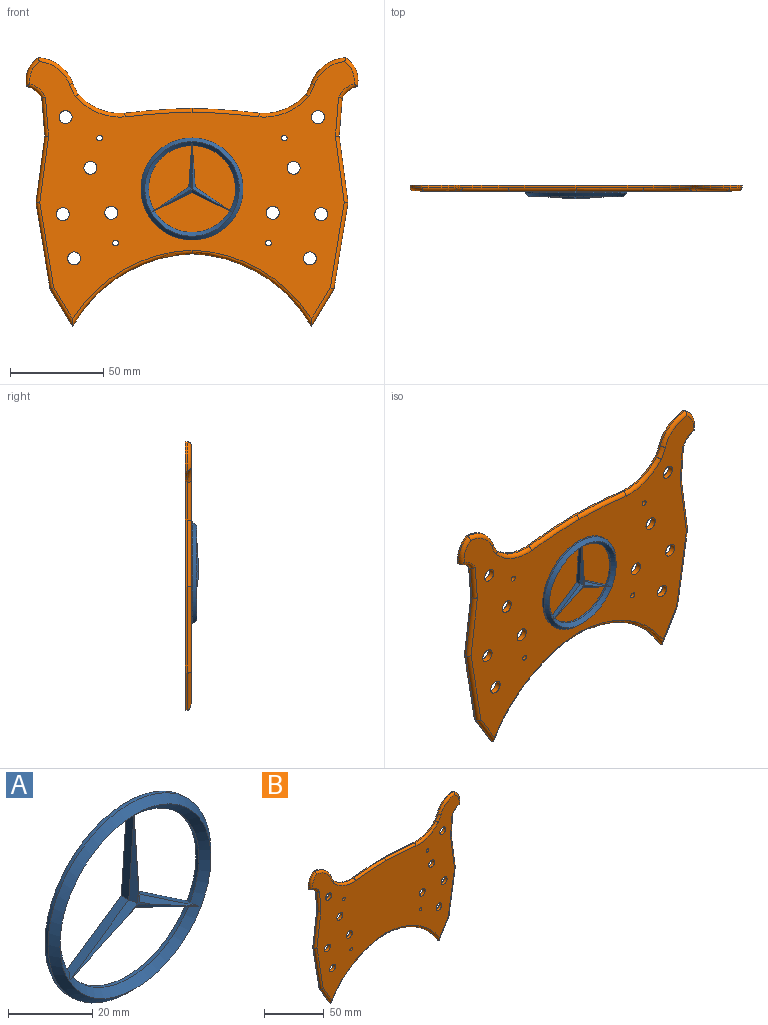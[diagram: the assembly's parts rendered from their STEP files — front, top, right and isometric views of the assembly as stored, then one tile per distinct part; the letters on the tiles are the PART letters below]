
ASSEMBLY  parts=2 mates=2
PART A: 20 faces, bbox 54.6x4x54.6 mm
  f0: cylinder r=23.31mm len=40.24mm, axis (0,1,0), area 48.5mm2, adj f4,f5,f9,f11
  f1: cylinder r=23.31mm len=34.85mm, axis (0,1,0), area 48.5mm2, adj f4,f5,f8,f10
  f2: cylinder r=23.31mm len=34.85mm, axis (0,1,0), area 48.5mm2, adj f4,f5,f7,f12
  f3: cylinder r=27.31mm len=54.63mm, axis (0,1,0), area 171.6mm2, adj f4,f6
  f4: plane 54.63x54.63mm, normal (0,1,0), area 766.9mm2, adj f0,f1,f2,f3,f7,f8,f9,f10
  f5: cone r=23.31mm half-angle=45deg, axis (0,-1,0), area 430.9mm2, adj f0,f1,f2,f6,f7,f8,f9,f10
  f6: cone r=25.31mm half-angle=45deg, axis (0,1,0), area 467.6mm2, adj f3,f5
  f7: plane 23.82x2.5mm, normal (1,0,0.07), area 57.1mm2, adj f2,f4,f5,f12,f17
  f8: plane 23.82x2.5mm, normal (-1,0,0.07), area 57.1mm2, adj f1,f4,f5,f10,f19
  f9: plane 21.48x10.44mm, normal (-0.44,0,-0.9), area 57.1mm2, adj f0,f4,f5,f11,f14
  f10: plane 19.78x13.38mm, normal (-0.56,0,0.83), area 57.1mm2, adj f1,f4,f5,f8,f18
  f11: plane 21.48x10.44mm, normal (0.44,0,-0.9), area 57.1mm2, adj f0,f4,f5,f9,f16
  f12: plane 19.78x13.38mm, normal (0.56,0,0.83), area 57.1mm2, adj f2,f4,f5,f7,f15
  f13: plane 7.28x6.31mm, normal (0,-1,0), area 3.6mm2, adj f14,f15,f16,f17,f18,f19
  f14: plane 21.52x12.11mm, normal (-0.31,-0.71,-0.64), area 30.1mm2, adj f5,f9,f13,f15,f16
  f15: plane 21.23x13.42mm, normal (0.4,-0.71,0.59), area 30.1mm2, adj f5,f12,f13,f14,f17
  f16: plane 21.52x12.11mm, normal (0.31,-0.71,-0.64), area 30.1mm2, adj f5,f11,f13,f14,f18
  f17: plane 24.68x1.73mm, normal (0.71,-0.71,0.05), area 30.1mm2, adj f5,f7,f13,f15,f19
  f18: plane 21.23x13.42mm, normal (-0.4,-0.71,0.59), area 30.1mm2, adj f5,f10,f13,f16,f19
  f19: plane 24.68x1.73mm, normal (-0.71,-0.71,0.05), area 30.1mm2, adj f5,f8,f13,f17,f18
PART B: 60 faces, bbox 180.3x3.4x145.7 mm
  f0: cylinder r=21.18mm len=18.59mm, axis (0,1,0), area 24.4mm2, adj f1,f21,f23,f43
  f1: cylinder r=14.27mm len=15.48mm, axis (0,1,0), area 17.8mm2, adj f0,f2,f23,f41
  f2: cylinder r=12.43mm len=8.03mm, axis (0,1,0), area 10.5mm2, adj f1,f3,f23,f39
  f3: plane 20.2x1.64mm, normal (-1,0,-0.08), area 20.3mm2, adj f2,f4,f23,f37
  f4: plane 35.67x4.72mm, normal (-0.99,0,0.13), area 36mm2, adj f3,f5,f23,f35
  f5: plane 46.36x7.54mm, normal (-0.99,0,-0.16), area 47mm2, adj f4,f6,f23,f33
  f6: plane 19.96x12.1mm, normal (-0.86,0,-0.52), area 23.3mm2, adj f5,f7,f23,f31
  f7: cylinder r=76.53mm len=63.97mm, axis (0,1,0), area 78.2mm2, adj f6,f8,f23,f29
  f8: cylinder r=76.53mm len=63.97mm, axis (0,1,0), area 78.2mm2, adj f7,f9,f23,f27
  f9: plane 19.96x12.1mm, normal (0.86,0,-0.52), area 23.3mm2, adj f8,f10,f23,f25
  f10: plane 46.36x7.54mm, normal (0.99,0,-0.16), area 47mm2, adj f9,f11,f23,f24
  f11: plane 35.67x4.72mm, normal (0.99,0,0.13), area 36mm2, adj f10,f12,f23,f26
  f12: plane 20.2x1.64mm, normal (1,0,-0.08), area 20.3mm2, adj f11,f13,f23,f28
  f13: cylinder r=12.43mm len=8.03mm, axis (0,1,0), area 10.5mm2, adj f12,f14,f23,f30
  f14: cylinder r=14.27mm len=15.48mm, axis (0,1,0), area 17.8mm2, adj f13,f15,f23,f32
  f15: cylinder r=21.18mm len=18.59mm, axis (0,1,0), area 24.4mm2, adj f14,f16,f23,f34
  f16: cylinder r=24.05mm len=5.87mm, axis (0,1,0), area 6.6mm2, adj f15,f17,f23,f36
  f17: cylinder r=29.8mm len=24.85mm, axis (0,1,0), area 27.9mm2, adj f16,f18,f23,f38
  f18: cylinder r=331.42mm len=36.04mm, axis (0,1,0), area 36.2mm2, adj f17,f19,f23,f40
  f19: cylinder r=331.42mm len=36.04mm, axis (0,1,0), area 36.2mm2, adj f18,f20,f23,f42
  f20: cylinder r=29.8mm len=24.85mm, axis (0,1,0), area 27.9mm2, adj f19,f21,f23,f44
  f21: cylinder r=24.05mm len=5.87mm, axis (0,1,0), area 6.6mm2, adj f0,f20,f23,f45
  f22: plane 173.95x138.02mm, normal (0,-1,0), area 14175.4mm2, adj f24,f25,f26,f27,f28,f29,f30,f31
  f23: plane 177.95x143.95mm, normal (0,1,0), area 15469.2mm2, adj f0,f1,f2,f3,f4,f5,f6,f7
  f24: cylinder r=2mm len=46.68mm, axis (-0.16,0,-0.99), area 146.8mm2, adj f10,f22,f25,f26
  f25: cylinder r=2mm len=21mm, axis (-0.52,0,-0.86), area 69mm2, adj f9,f22,f24,f27
  f26: cylinder r=2mm len=36.14mm, axis (0.13,0,-0.99), area 112.9mm2, adj f11,f22,f24,f28
  f27: torus R=78.53mm, axis (0,-1,0), area 244.2mm2, adj f8,f22,f25,f29
  f28: cylinder r=2mm len=20.96mm, axis (-0.08,0,-1), area 64.4mm2, adj f12,f22,f26,f30
  f29: torus R=78.53mm, axis (0,-1,0), area 244.2mm2, adj f7,f22,f27,f31
  f30: torus R=14.43mm, axis (0,-1,0), area 34mm2, adj f13,f22,f28,f32
  f31: cylinder r=2mm len=21mm, axis (-0.52,0,0.86), area 69mm2, adj f6,f22,f29,f33
  f32: torus R=12.27mm, axis (0,-1,0), area 51mm2, adj f14,f22,f30,f34
  f33: cylinder r=2mm len=46.68mm, axis (-0.16,0,0.99), area 146.8mm2, adj f5,f22,f31,f35
  f34: torus R=19.18mm, axis (0,-1,0), area 73.3mm2, adj f15,f22,f32,f36
  f35: cylinder r=2mm len=36.14mm, axis (0.13,0,0.99), area 112.9mm2, adj f4,f22,f33,f37
  f36: torus R=26.05mm, axis (0,-1,0), area 21.4mm2, adj f16,f22,f34,f38
  f37: cylinder r=2mm len=20.96mm, axis (-0.08,0,1), area 64.4mm2, adj f3,f22,f35,f39
  f38: torus R=31.8mm, axis (0,-1,0), area 89.9mm2, adj f17,f22,f36,f40
  f39: torus R=14.43mm, axis (0,-1,0), area 34mm2, adj f2,f22,f37,f41
  f40: torus R=329.42mm, axis (0,-1,0), area 113.3mm2, adj f18,f22,f38,f42
  f41: torus R=12.27mm, axis (0,-1,0), area 51mm2, adj f1,f22,f39,f43
  f42: torus R=329.42mm, axis (0,-1,0), area 113.3mm2, adj f19,f22,f40,f44
  f43: torus R=19.18mm, axis (0,-1,0), area 73.3mm2, adj f0,f22,f41,f45
  f44: torus R=31.8mm, axis (0,-1,0), area 89.9mm2, adj f20,f22,f42,f45
  f45: torus R=26.05mm, axis (0,-1,0), area 21.4mm2, adj f21,f22,f43,f44
  f46: cylinder r=1.5mm len=3mm, axis (0,1,0), area 28.3mm2, adj f22,f23
  f47: cylinder r=1.5mm len=3mm, axis (0,1,0), area 28.3mm2, adj f22,f23
  f48: cylinder r=1.5mm len=3mm, axis (0,1,0), area 28.3mm2, adj f22,f23
  f49: cylinder r=1.5mm len=3mm, axis (0,1,0), area 28.3mm2, adj f22,f23
  f50: cylinder r=3.5mm len=7mm, axis (0,1,0), area 66mm2, adj f22,f23
  f51: cylinder r=3.5mm len=7mm, axis (0,1,0), area 66mm2, adj f22,f23
  f52: cylinder r=3.5mm len=7mm, axis (0,1,0), area 66mm2, adj f22,f23
  f53: cylinder r=3.5mm len=7mm, axis (0,1,0), area 66mm2, adj f22,f23
  f54: cylinder r=3.5mm len=7mm, axis (0,1,0), area 66mm2, adj f22,f23
  f55: cylinder r=3.5mm len=7mm, axis (0,1,0), area 66mm2, adj f22,f23
  f56: cylinder r=3.5mm len=7mm, axis (0,1,0), area 66mm2, adj f22,f23
  f57: cylinder r=3.5mm len=7mm, axis (0,1,0), area 66mm2, adj f22,f23
  f58: cylinder r=3.5mm len=7mm, axis (0,1,0), area 66mm2, adj f22,f23
  f59: cylinder r=3.5mm len=7mm, axis (0,1,0), area 66mm2, adj f22,f23
PLACE A t=(4.03,47.64,96.39)mm
PLACE B t=(4.03,50.64,103.01)mm
MATE planar A.f3 <-> B.f22  axis (0,1,0) through (4.03,47.64,96.39)mm
MATE planar B.f51 <-> B.f51  axis (0,-1,0) through (58.5,47.64,107.73)mm
